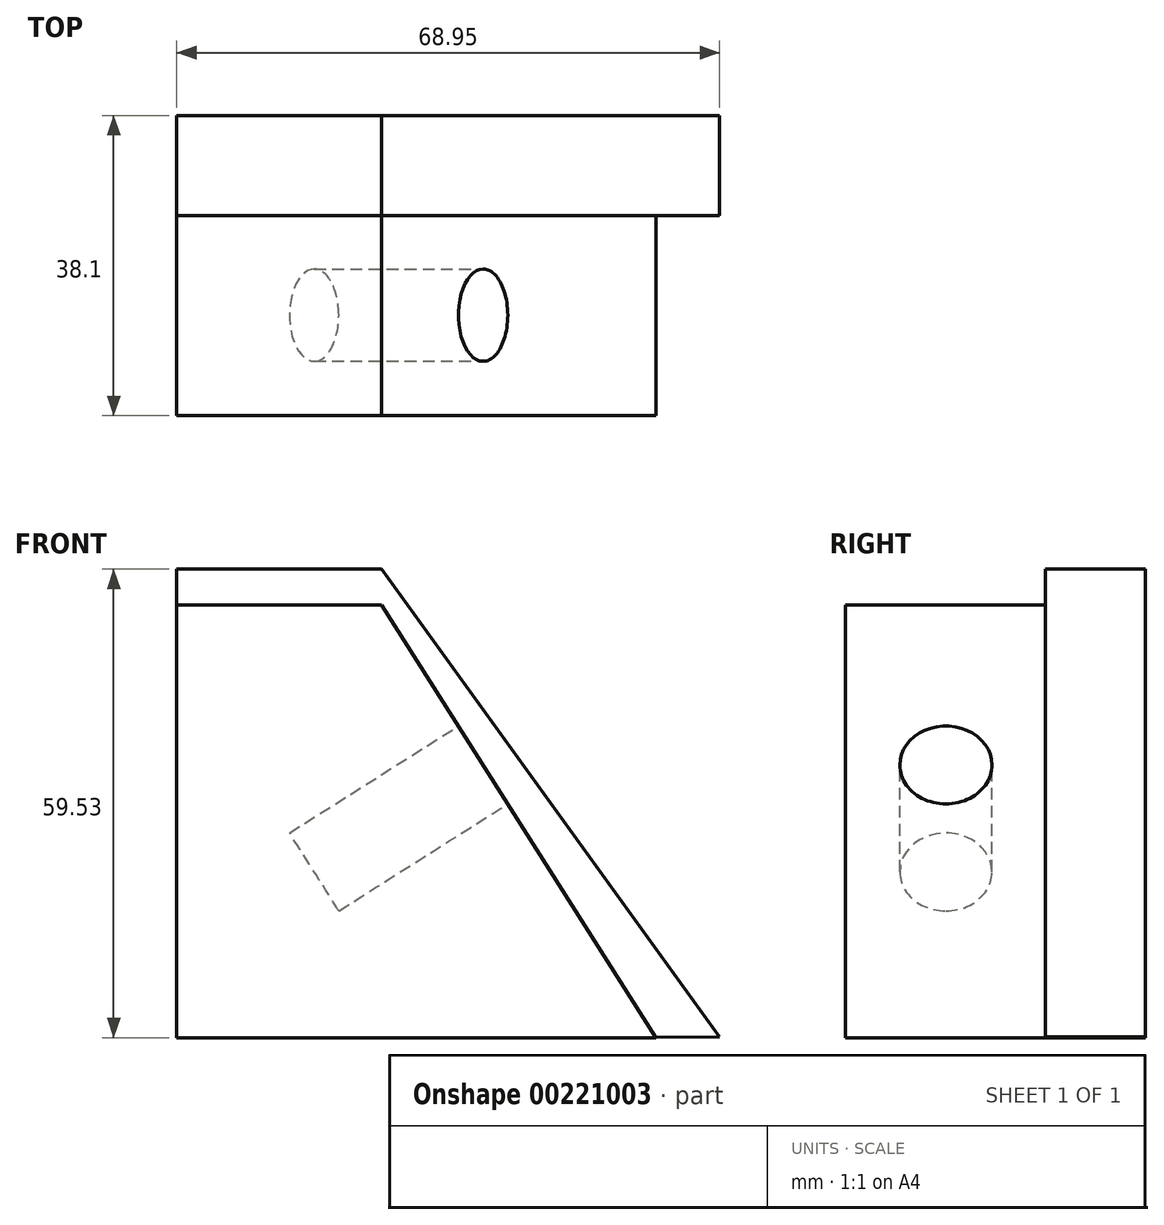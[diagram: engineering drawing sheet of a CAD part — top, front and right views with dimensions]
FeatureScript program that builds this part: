
annotation { "Feature Type Name" : "Feature", "Feature Type Description" : "" }
export const myFeature = defineFeature(function(context is Context, id is Id, definition is map)
    precondition{}
    {
        {
            var Q0;
            Q0=qCreatedBy(makeId("Front.planeOp"),FACE);
            var sketch = newSketch(context, id + "F0", { "sketchPlane" : qUnion([Q0])});
            skLineSegment(sketch, "E0.bottom", {"start": v(-44.54, 32.72) * mm, "end": v(48.76, 32.72) * mm});
            skLineSegment(sketch, "E0.top", {"start": v(-44.54, -22.27) * mm, "end": v(48.76, -22.27) * mm});
            skLineSegment(sketch, "E0.left", {"start": v(-44.54, 32.72) * mm, "end": v(-44.54, -22.27) * mm});
            skLineSegment(sketch, "E0.right", {"start": v(48.76, 32.72) * mm, "end": v(48.76, -22.27) * mm});
            skSolve(sketch);
        }
        {
            var Q0;
            Q0 = qSketchRegion(id + "F0", true);
            extrude(context, id + "F1", {"entities" : qUnion([Q0]), "depth" : 25.4 * mm});
        }
        {
            var Q0;
            Q0=makeQuery(id+"F1.opExtrude","CAP_FACE",FACE,{"disambiguationData":[OSD([sQuery(id+"F0.wireOp",EDGE,"E0.bottom"),sQuery(id+"F0.wireOp",EDGE,"E0.top"),sQuery(id+"F0.wireOp",EDGE,"E0.left"),sQuery(id+"F0.wireOp",EDGE,"E0.right")])],"isStart":false});
            var sketch = newSketch(context, id + "F2", { "sketchPlane" : qUnion([Q0])});
            skLineSegment(sketch, "E1", {"start": v(-18.51, 32.72) * mm, "end": v(16.31, -22.27) * mm});
            skLineSegment(sketch, "E2", {"start": v(-18.51, 32.72) * mm, "end": v(55.54, 35.29) * mm});
            skLineSegment(sketch, "E3", {"start": v(16.31, -22.27) * mm, "end": v(61.22, -24.65) * mm});
            skLineSegment(sketch, "E4", {"start": v(55.54, 35.29) * mm, "end": v(61.22, -24.65) * mm});
            skSolve(sketch);
        }
        {
            var Q0;
            Q0 = qSketchRegion(id + "F2", true);
            extrude(context, id + "F3", {"entities" : qUnion([Q0]), "operationType" : NewBodyOperationType.REMOVE, "oppositeDirection" : true, "depth" : 25.4 * mm});
        }
        {
            var Q0;
            Q0=makeQuery(id+"F3.boolean.opBoolean","COPY",FACE,{"derivedFrom":makeQuery(id+"F3.opExtrude","SWEPT_FACE",FACE,{"disambiguationData":[OSD([sQuery(id+"F2.wireOp",EDGE,"E1")])]})});
            var sketch = newSketch(context, id + "F4", { "sketchPlane" : qUnion([Q0])});
            skCircle(sketch, "E5", {"center": v(-12.65, 13.46) * mm, "radius": 5.86 * mm});
            skSolve(sketch);
        }
        {
            var Q0;
            Q0 = qSketchRegion(id + "F4", true);
            extrude(context, id + "F5", {"entities" : qUnion([Q0]), "operationType" : NewBodyOperationType.REMOVE, "oppositeDirection" : true, "depth" : 25.4 * mm});
        }
        {
            var Q0;
            Q0=qCreatedBy(makeId("Front.planeOp"),FACE);
            var sketch = newSketch(context, id + "F6", { "sketchPlane" : qUnion([Q0])});
            skLineSegment(sketch, "E6.bottom", {"start": v(35.2, 32.72) * mm, "end": v(-44.9, 32.72) * mm});
            skLineSegment(sketch, "E6.top", {"start": v(35.2, -22.64) * mm, "end": v(-44.9, -22.64) * mm});
            skLineSegment(sketch, "E6.left", {"start": v(35.2, 32.72) * mm, "end": v(35.2, -22.64) * mm});
            skLineSegment(sketch, "E6.right", {"start": v(-44.9, 32.72) * mm, "end": v(-44.9, -22.64) * mm});
            skSolve(sketch);
        }
        {
            var Q0;
            Q0=makeQuery(id+"F6.imprint","IMPRINT",FACE,{"disambiguationData":[TD([[makeQuery(id+"F6.imprint","IMPRINT",EDGE,{"derivedFrom":sQuery(id+"F6.wireOp",EDGE,"E6.bottom")}),1.0]])]});
            extrude(context, id + "F7", {"entities" : qUnion([Q0]), "operationType" : NewBodyOperationType.REMOVE, "oppositeDirection" : true, "depth" : 25.4 * mm});
        }
        {
            var Q0;
            Q0=makeQuery(id+"F1.opExtrude","CAP_FACE",FACE,{"disambiguationData":[OSD([sQuery(id+"F0.wireOp",EDGE,"E0.bottom"),sQuery(id+"F0.wireOp",EDGE,"E0.top"),sQuery(id+"F0.wireOp",EDGE,"E0.left"),sQuery(id+"F0.wireOp",EDGE,"E0.right")])],"isStart":true});
            var sketch = newSketch(context, id + "F8", { "sketchPlane" : qUnion([Q0])});
            skLineSegment(sketch, "E7", {"start": v(18.51, 37.26) * mm, "end": v(18.51, 32.72) * mm});
            skLineSegment(sketch, "E8", {"start": v(18.51, 37.26) * mm, "end": v(-24.4, -22.2) * mm});
            skLineSegment(sketch, "E9", {"start": v(-24.4, -22.2) * mm, "end": v(44.54, -22.27) * mm});
            skLineSegment(sketch, "E10", {"start": v(18.51, 37.26) * mm, "end": v(44.54, 37.26) * mm});
            skLineSegment(sketch, "E11", {"start": v(44.54, 37.26) * mm, "end": v(44.54, -22.27) * mm});
            skSolve(sketch);
        }
        {
            var Q0;
            Q0 = qSketchRegion(id + "F8", true);
            extrude(context, id + "F9", {"entities" : qUnion([Q0]), "operationType" : NewBodyOperationType.ADD, "depth" : 12.7 * mm});
        }
    });
